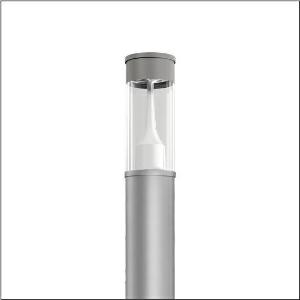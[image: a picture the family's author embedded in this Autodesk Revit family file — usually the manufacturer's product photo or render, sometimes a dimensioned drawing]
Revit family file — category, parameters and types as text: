
# Revit family: city-light_260_iq___pl1_2s_5xa5295rf14h_a018
name_source: partatom
category: Lighting Fixtures
units: mm (PartAtom-declared; Revit-internal decimal feet)

## family parameters
Cut with Voids When Loaded = No
Host = Face
Light Source = No
Part Type = Normal
Room Calculation Point = No
Round Connector Dimension = Use Diameter
Shared = No

## types (1)
- --- (1 x LED, 2970 lm, 18.5 W, 4000K)
    Apparent Load = 19 VA
    CIE Flux Codes = 23 62 94 96 100
    Color Rendering = 70
    Color Temperature = 4000K
    Default Elevation = 1800 mm
    Description = City-Light 260 iQ, light pillar, Module 540 iQ-SR, primary light control with 3 zone facetted reflector, of plastic, silver coated, highly specular, structured, primary optical cover: cover, of PMMA, transparent, partly coated, light distribution: PL1.2s, primary light characteristic: symmetric, LED, High Power LED, rated luminous flux: 2.970lm, luminous efficacy: 161lm/W, light colour: 740, colour temperature: 4000K, control gear: ECG iQ, control: pre-setting: logarithmic dimming characteristic, Street-Remote, Auto-Match, Temp-Guard, Lumen-Switch, Night-Set, Smart-Wire, Light-Fading, Desk-Remote (wireless, voltage-free reading and setting of iQ features in the workshop via application-optimized NFC function/RFID function), optimised constant luminous flux control (CLO 2.0), with terminal, 6-pole, max. 2.5mm², mains connection: 230..240V, AC, 50/60Hz, start of lifetime: 19W, end of service life: 20W, reduction: 9W, luminaire housing, cylindrical, of extruded aluminium section, coated, Siteco® metallic grey (DB 702S), length: 2.600mm, diameter: 200mm, Module 540 iQ-SR, traffic white (RAL 9016), equipment: standard, protection rating (complete): IP65, insulation class (complete): insulation class II (safety insulation), certification: CE, ENEC, VDE, packaging unit: 1 piece

Light Distribution: PL1.2s
    Height = 500 mm
    Lamp = 1 x LED
    Lamp Light Flux = 2970 lm
    Lamp Power = 18.5 W
    Lamp count = 1
    Length = 200 mm  [stored 0.656168 ft]
    Luminous efficacy = 161 lm/W
    Manufacturer = Siteco
    ModVariant = No
    Model = 5XA5295RF14H
    Mounting Place = Floor
    Mounting Type = Freestanding
    Number of Poles = 1
    OnlyDefault = Yes
    Power Factor = 1
    Product Name = City-Light 260 iQ | PL1.2s
    Product group = light pillar
    ProductGroupID = 1301
    Protection Class = Protection class II
    Protection Degree = IP 65
    RLX_Detail_Level = 1
    RLX_Emergency_Light_Flux = 0 lm
    RLX_Emergency_Type = 0
    RLX_Emergency_Type_DB = No
    RlxData = <blob elided: 28721 chars, md5=6252ccd3>
    Socket = socket
    Standby Power = 0 W
    System Light Flux = 2970 lm
    System Power = 19 W
    Type Comments = factory setting: luminous flux: 100 % | dim-lin: 254 | 385 mA
    Type Image = l_1006920.jpg
    URL = http://relux.com
    VarID = @adj_114977
    Voltage = 0 V
    Weight = 0.00 kg
    Width = 0 mm  [stored 0 ft]

note: [stored X ft] marks values corroborated as IEEE doubles in the binary element streams (Revit-internal decimal feet)

## geometry (parser evidence)
native form markers: Blend x4, Sweep x11
no freeform markers — native parametric forms only
